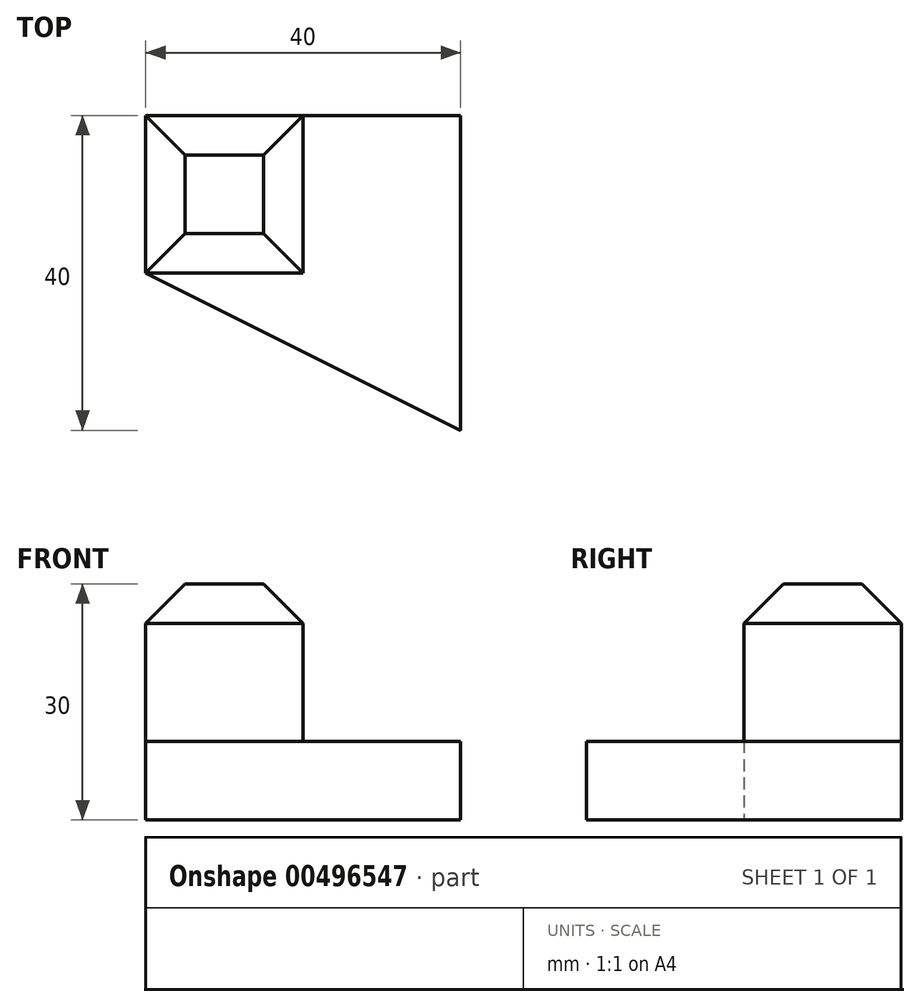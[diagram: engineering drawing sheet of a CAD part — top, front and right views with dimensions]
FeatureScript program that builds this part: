
annotation { "Feature Type Name" : "Feature", "Feature Type Description" : "" }
export const myFeature = defineFeature(function(context is Context, id is Id, definition is map)
    precondition{}
    {
        {
            var Q0;
            Q0=qCreatedBy(makeId("Top.planeOp"),FACE);
            var sketch = newSketch(context, id + "F0", { "sketchPlane" : qUnion([Q0])});
            skLineSegment(sketch, "E0", {"start": v(0, 0) * mm, "end": v(0, 20) * mm});
            skLineSegment(sketch, "E1", {"start": v(0, 20) * mm, "end": v(40, 20) * mm});
            skLineSegment(sketch, "E2", {"start": v(40, 20) * mm, "end": v(40, -20) * mm});
            skLineSegment(sketch, "E3", {"start": v(0, 0) * mm, "end": v(40, -20) * mm});
            skSolve(sketch);
        }
        {
            var Q0;
            Q0=qSketchRegion(id+"F0",true);
            extrude(context, id + "F1", {"entities" : qUnion([Q0]), "depth" : 10 * mm});
        }
        {
            var Q0;
            Q0=makeQuery(id+"F1.opExtrude","CAP_FACE",FACE,{"disambiguationData":[OSD([sQuery(id+"F0.wireOp",EDGE,"E0"),sQuery(id+"F0.wireOp",EDGE,"E1"),sQuery(id+"F0.wireOp",EDGE,"E2"),sQuery(id+"F0.wireOp",EDGE,"E3")])],"isStart":false});
            var sketch = newSketch(context, id + "F2", { "sketchPlane" : qUnion([Q0])});
            skLineSegment(sketch, "E4", {"start": v(0, 0) * mm, "end": v(20, 0) * mm});
            skLineSegment(sketch, "E5", {"start": v(20, 0) * mm, "end": v(20, 20) * mm});
            skSolve(sketch);
        }
        {
            var Q0;
            Q0=makeQuery(id+"F2.imprint","IMPRINT",FACE,{"disambiguationData":[TD([[makeQuery(id+"F2.imprint","IMPRINT",EDGE,{"derivedFrom":sQuery(id+"F2.wireOp",EDGE,"E4")}),1.0]])]});
            extrude(context, id + "F3", {"entities" : qUnion([Q0]), "operationType" : NewBodyOperationType.ADD, "depth" : 20 * mm});
        }
        {
            var Q0;
            Q0=makeQuery(id+"F3.opExtrude","CAP_FACE",FACE,{"disambiguationData":[OSD([sQuery(id+"F0.wireOp",EDGE,"E0"),sQuery(id+"F0.wireOp",EDGE,"E1"),sQuery(id+"F2.wireOp",EDGE,"E4"),sQuery(id+"F2.wireOp",EDGE,"E5")])],"isStart":false});
            chamfer(context, id + "F4", {"entities" : qUnion([Q0]), "width" : 5 * mm, "tangentPropagation" : true});
        }
    });
